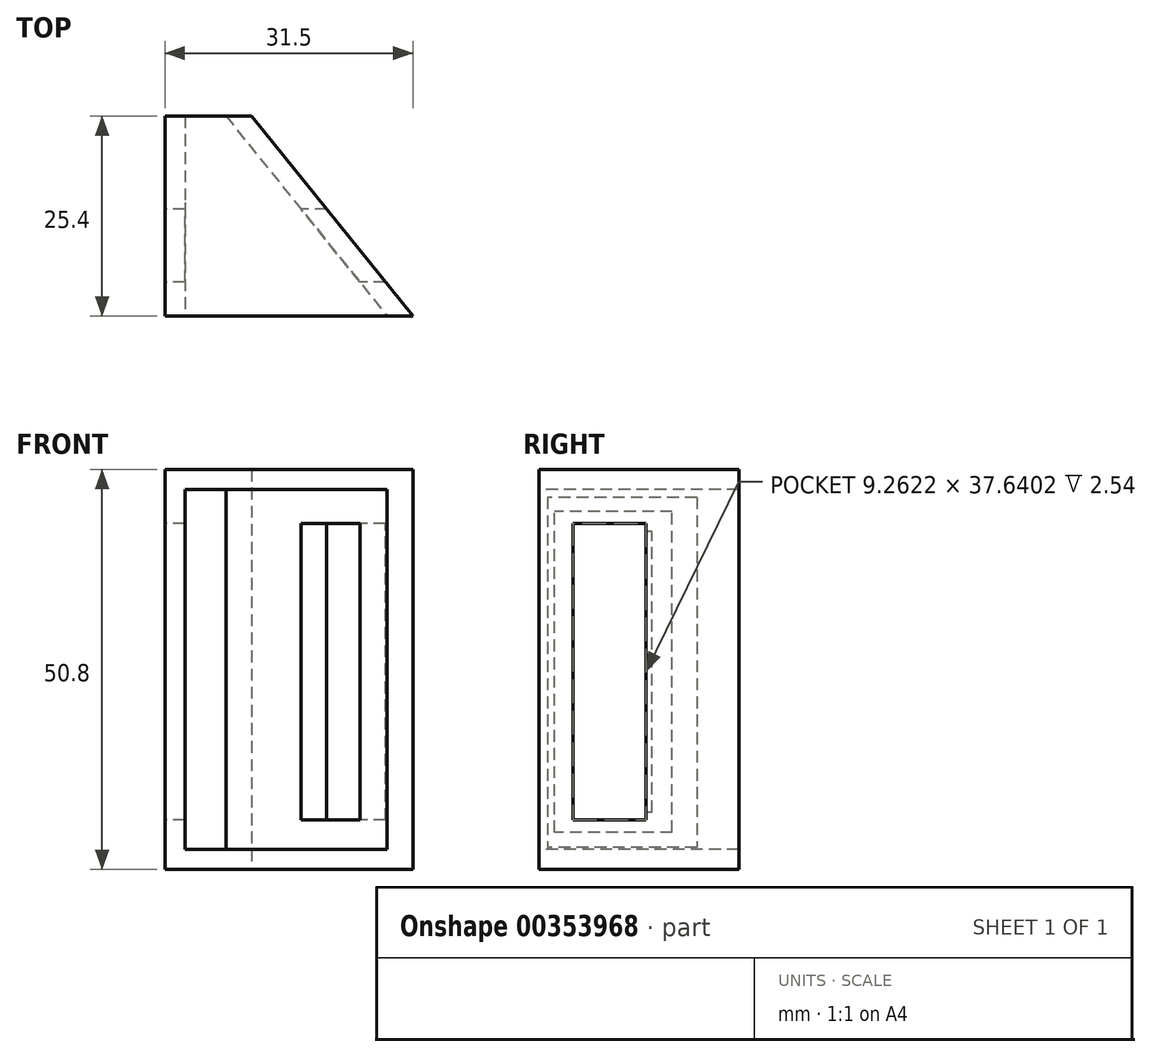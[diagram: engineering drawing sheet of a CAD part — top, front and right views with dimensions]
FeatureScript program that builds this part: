
annotation { "Feature Type Name" : "Feature", "Feature Type Description" : "" }
export const myFeature = defineFeature(function(context is Context, id is Id, definition is map)
    precondition{}
    {
        {
            var Q0;
            Q0=qCreatedBy(makeId("Top.planeOp"),FACE);
            var sketch = newSketch(context, id + "F0", { "sketchPlane" : qUnion([Q0])});
            skLineSegment(sketch, "E0", {"start": v(-15.93, 15.96) * mm, "end": v(-15.93, -9.44) * mm});
            skLineSegment(sketch, "E1", {"start": v(-15.93, -9.44) * mm, "end": v(15.57, -9.44) * mm});
            skLineSegment(sketch, "E2", {"start": v(-15.93, 15.96) * mm, "end": v(-4.93, 15.96) * mm});
            skLineSegment(sketch, "E3", {"start": v(-4.93, 15.96) * mm, "end": v(15.57, -9.44) * mm});
            skSolve(sketch);
        }
        {
            var Q0;
            Q0=qSketchRegion(id+"F0",true);
            extrude(context, id + "F1", {"entities" : qUnion([Q0]), "endBound" : BoundingType.SYMMETRIC, "depth" : 50.8 * mm});
        }
        {
            var Q0;
            Q0=makeQuery(id+"F1.opExtrude","SWEPT_FACE",FACE,{"disambiguationData":[OSD([sQuery(id+"F0.wireOp",EDGE,"E0")])]});
            var sketch = newSketch(context, id + "F2", { "sketchPlane" : qUnion([Q0])});
            skLineSegment(sketch, "E4.bottom", {"start": v(-7.49, -20.7) * mm, "end": v(7.49, -20.7) * mm});
            skLineSegment(sketch, "E4.top", {"start": v(-7.49, 20.1) * mm, "end": v(7.49, 20.1) * mm});
            skLineSegment(sketch, "E4.left", {"start": v(-7.49, -20.7) * mm, "end": v(-7.49, 20.1) * mm});
            skLineSegment(sketch, "E4.right", {"start": v(7.49, -20.7) * mm, "end": v(7.49, 20.1) * mm});
            skSolve(sketch);
        }
        {
            var Q0;
            Q0=qSketchRegion(id+"F2",true);
            extrude(context, id + "F3", {"entities" : qUnion([Q0]), "operationType" : NewBodyOperationType.ADD, "depth" : 0 * mm});
        }
        {
            var Q0;
            Q0=makeQuery(id+"F1.opExtrude","SWEPT_FACE",FACE,{"disambiguationData":[OSD([sQuery(id+"F0.wireOp",EDGE,"E2")])]});
            var Q1;
            Q1=makeQuery(id+"F1.opExtrude","SWEPT_FACE",FACE,{"disambiguationData":[OSD([sQuery(id+"F0.wireOp",EDGE,"E1")])]});
            shell(context, id + "F4", {"entities" : qUnion([Q0, Q1]), "thickness" : 2.54 * mm});
        }
        {
            var Q0;
            Q0=makeQuery(id+"F1.opExtrude","SWEPT_FACE",FACE,{"disambiguationData":[OSD([sQuery(id+"F0.wireOp",EDGE,"E0")])]});
            var sketch = newSketch(context, id + "F5", { "sketchPlane" : qUnion([Q0])});
            skLineSegment(sketch, "E5.bottom", {"start": v(-4.14, 18.52) * mm, "end": v(5.12, 18.52) * mm});
            skLineSegment(sketch, "E5.top", {"start": v(-4.14, -19.12) * mm, "end": v(5.12, -19.12) * mm});
            skLineSegment(sketch, "E5.left", {"start": v(-4.14, 18.52) * mm, "end": v(-4.14, -19.12) * mm});
            skLineSegment(sketch, "E5.right", {"start": v(5.12, 18.52) * mm, "end": v(5.12, -19.12) * mm});
            skSolve(sketch);
        }
        {
            var Q0;
            Q0 = qSketchRegion(id + "F5", true);
            extrude(context, id + "F6", {"entities" : qUnion([Q0]), "operationType" : NewBodyOperationType.REMOVE, "oppositeDirection" : true, "depth" : 194.82 * mm});
        }
        {
            var Q0;
            Q0=makeQuery(id+"F1.opExtrude","SWEPT_FACE",FACE,{"disambiguationData":[OSD([sQuery(id+"F0.wireOp",EDGE,"E0")])]});
            var sketch = newSketch(context, id + "F7", { "sketchPlane" : qUnion([Q0])});
            skLineSegment(sketch, "E6.bottom", {"start": v(-10.64, 21.87) * mm, "end": v(8.38, 21.87) * mm});
            skLineSegment(sketch, "E6.top", {"start": v(-10.64, -22.62) * mm, "end": v(8.38, -22.62) * mm});
            skLineSegment(sketch, "E6.left", {"start": v(-10.64, 21.87) * mm, "end": v(-10.64, -22.62) * mm});
            skLineSegment(sketch, "E6.right", {"start": v(8.38, 21.87) * mm, "end": v(8.38, -22.62) * mm});
            skSolve(sketch);
        }
        {
            var Q0;
            Q0 = qSketchRegion(id + "F7", true);
            extrude(context, id + "F8", {"entities" : qUnion([Q0]), "operationType" : NewBodyOperationType.ADD, "depth" : 0 * mm});
        }
    });
